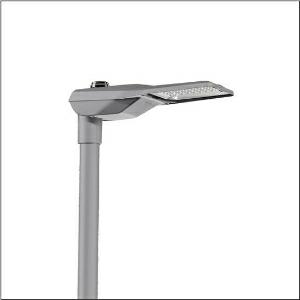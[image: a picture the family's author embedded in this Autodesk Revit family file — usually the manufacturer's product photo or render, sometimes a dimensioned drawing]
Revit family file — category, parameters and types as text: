
# Revit family: streetlight_sl_21_mini___p0_8a_5xe6u57n08hb_6fdb
name_source: partatom
category: Lighting Fixtures
units: mm (PartAtom-declared; Revit-internal decimal feet)

## family parameters
Cut with Voids When Loaded = No
Host = Face
Light Source = No
Part Type = Normal
Room Calculation Point = No
Round Connector Dimension = Use Diameter
Shared = No

## types (1)
- --- (1 x LED, 7850 lm, 66 W, 3000K)
    Apparent Load = 66 VA
    CIE Flux Codes = 33 69 96 100 100
    Color Rendering = 80
    Color Temperature = 3000K
    Default Elevation = 1800 mm
    Description = Streetlight SL 21 mini, mast luminaire, primary light control with lens, of PMMA, primary optical cover: cover, of toughened safety glass, transparent, light distribution: P0.8a, light emission: direct distribution, primary light characteristic: asymmetric, installation type: side-entry, LED, 3G 1.5mm², High Power LED, rated luminous flux: 7.850lm, luminous efficacy: 119lm/W, light colour: 830, colour temperature: 3000K, control gear: NEMA (7pin), control: flexible luminous flux parameterisation, time-dependent luminous flux control, constant luminous flux control, pre-setting: linear dimming characteristic, overheat protection, mains connection: 230..240V, AC, 50/60Hz, connection cable pre-assembled, cable length: 8,5m, wiring characteristics: H07RN-F, start of lifetime: 66W, end of service life: 69W, reduction: 30W, luminaire housing, of diecast aluminium (EN AC-44300), powder-coated, Siteco® metallic grey (DB 702S), corrosivity category C5 mid according to DIN EN ISO 12944, multi-level sealing system, sealing non-destructively replaceable, inclination adjustable: 0°, 5°, 10°, 15°, length: 628mm, width: 235mm, height: 110mm, spigot size: 42mm (side-entry), mounting height: 4..8m, protection rating (complete): IP66, insulation class (complete): insulation class I (protective earthing), certification: CE, ENEC, ENEC+, VDE, impact resistance: IK10, permissible operating ambient temperature for outdoor applications: -40..+50°C, standard-compliant lighting for roads and squares, packaging unit: 1 piece

Light Distribution: P0.8a
    Height = 110 mm
    Lamp = 1 x LED
    Lamp Light Flux = 7850 lm
    Lamp Power = 66 W
    Lamp count = 1
    Length = 625 mm
    Luminous efficacy = 119 lm/W
    Manufacturer = Siteco
    ModVariant = No
    Model = 5XE6U57N08HB
    Number of Poles = 1
    OnlyDefault = Yes
    Power Factor = 1
    Product Name = Streetlight SL 21 mini | P0.8a
    Product group = mast luminaire | pylon top
    ProductGroupID = 6100
    Protection Class = Protection class I
    Protection Degree = IP 66
    RLX_Detail_Level = 1
    RLX_Emergency_Light_Flux = 0 lm
    RLX_Emergency_Type = 0
    RLX_Emergency_Type_DB = No
    RlxData = <blob elided: 91761 chars, md5=f88e87f3>
    Socket = socket
    Standby Power = 0 W
    System Light Flux = 7850 lm
    System Power = 66 W
    Type Comments = factory setting: luminous flux: 100 % | dim-lin: 254 | 670 mA
    Type Image = l_1294379.jpg
    URL = http://relux.com
    VarID = @adj_094987
    Voltage = 0 V
    Weight = 0.00 kg
    Width = 234 mm

## geometry (parser evidence)
native form markers: Blend x4, Sweep x11
no freeform markers — native parametric forms only
